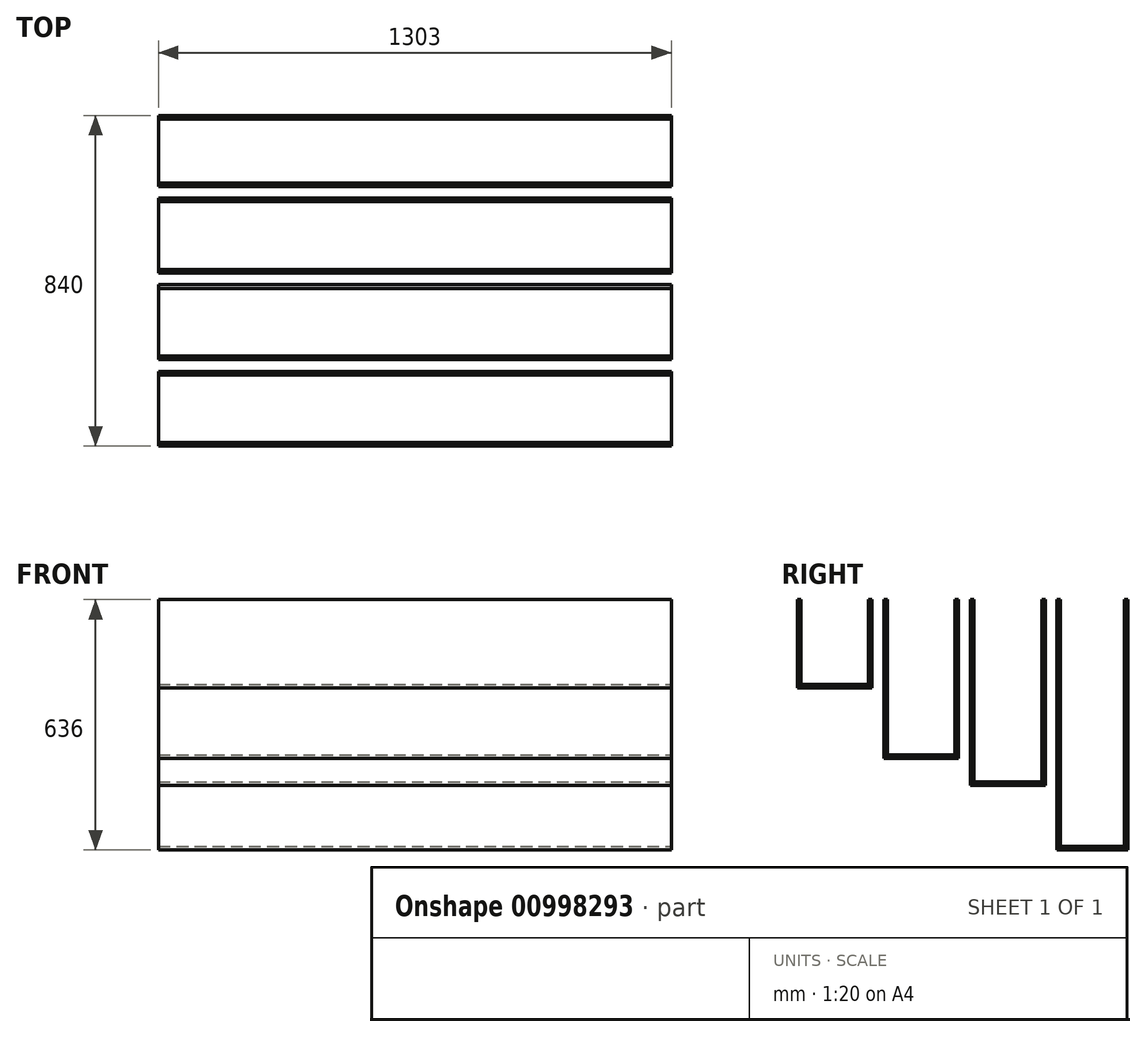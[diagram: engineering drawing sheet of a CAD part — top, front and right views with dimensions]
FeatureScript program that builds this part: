
annotation { "Feature Type Name" : "Feature", "Feature Type Description" : "" }
export const myFeature = defineFeature(function(context is Context, id is Id, definition is map)
    precondition{}
    {
        {
            var Q0;
            Q0=qCreatedBy(makeId("Right.planeOp"),FACE);
            var sketch = newSketch(context, id + "F0", { "sketchPlane" : qUnion([Q0])});
            skLineSegment(sketch, "E0.bottom", {"start": v(-47.02, 266.3) * mm, "end": v(-38.02, 266.3) * mm});
            skLineSegment(sketch, "E0.top", {"start": v(-47.02, 42.3) * mm, "end": v(-38.02, 42.3) * mm});
            skLineSegment(sketch, "E0.left", {"start": v(-47.02, 266.3) * mm, "end": v(-47.02, 42.3) * mm});
            skLineSegment(sketch, "E0.right", {"start": v(-38.02, 266.3) * mm, "end": v(-38.02, 42.3) * mm});
            skSolve(sketch);
        }
        {
            var Q0;
            Q0 = qSketchRegion(id + "F0", true);
            extrude(context, id + "F1", {"entities" : qUnion([Q0]), "oppositeDirection" : true, "depth" : 1303 * mm, "offsetDistance" : 25 * mm});
        }
        {
            var Q0;
            Q0=qCreatedBy(makeId("Right.planeOp"),FACE);
            var sketch = newSketch(context, id + "F2", { "sketchPlane" : qUnion([Q0])});
            skLineSegment(sketch, "E1.0.0", {"start": v(-47.02, 266.3) * mm, "end": v(-47.02, 42.3) * mm, "construction": true});
            skLineSegment(sketch, "E1.0.1", {"start": v(-47.02, 42.3) * mm, "end": v(-38.02, 42.3) * mm, "construction": true});
            skLineSegment(sketch, "E1.0.2", {"start": v(-38.02, 42.3) * mm, "end": v(-38.02, 266.3) * mm, "construction": true});
            skLineSegment(sketch, "E1.0.3", {"start": v(-38.02, 266.3) * mm, "end": v(-47.02, 266.3) * mm, "construction": true});
            skLineSegment(sketch, "E2.bottom", {"start": v(-38.02, 42.3) * mm, "end": v(133.98, 42.3) * mm});
            skLineSegment(sketch, "E2.top", {"start": v(-38.02, 51.3) * mm, "end": v(133.98, 51.3) * mm});
            skLineSegment(sketch, "E2.left", {"start": v(-38.02, 42.3) * mm, "end": v(-38.02, 51.3) * mm});
            skLineSegment(sketch, "E2.right", {"start": v(133.98, 42.3) * mm, "end": v(133.98, 51.3) * mm});
            skSolve(sketch);
        }
        {
            var Q0;
            Q0 = qSketchRegion(id + "F2", true);
            var Q1;
            Q1=makeQuery(id+"F1.opExtrude","CAP_FACE",FACE,{"disambiguationData":[OSD([sQuery(id+"F0.wireOp",EDGE,"E0.bottom"),sQuery(id+"F0.wireOp",EDGE,"E0.top"),sQuery(id+"F0.wireOp",EDGE,"E0.left"),sQuery(id+"F0.wireOp",EDGE,"E0.right")])],"isStart":false});
            extrude(context, id + "F3", {"entities" : qUnion([Q0]), "endBound" : BoundingType.UP_TO_SURFACE, "oppositeDirection" : true, "depth" : 1303 * mm, "endBoundEntityFace" : qUnion([Q1]), "offsetDistance" : 25 * mm});
        }
        {
            var Q0;
            Q0=qCreatedBy(makeId("Right.planeOp"),FACE);
            var sketch = newSketch(context, id + "F4", { "sketchPlane" : qUnion([Q0])});
            skLineSegment(sketch, "E3.0.0", {"start": v(133.98, 51.3) * mm, "end": v(-38.02, 51.3) * mm, "construction": true});
            skLineSegment(sketch, "E3.0.1", {"start": v(-38.02, 51.3) * mm, "end": v(-38.02, 42.3) * mm, "construction": true});
            skLineSegment(sketch, "E3.0.2", {"start": v(-38.02, 42.3) * mm, "end": v(133.98, 42.3) * mm, "construction": true});
            skLineSegment(sketch, "E3.0.3", {"start": v(133.98, 42.3) * mm, "end": v(133.98, 51.3) * mm, "construction": true});
            skLineSegment(sketch, "E4.bottom", {"start": v(133.98, 42.3) * mm, "end": v(142.98, 42.3) * mm});
            skLineSegment(sketch, "E4.top", {"start": v(133.98, 266.3) * mm, "end": v(142.98, 266.3) * mm});
            skLineSegment(sketch, "E4.left", {"start": v(133.98, 42.3) * mm, "end": v(133.98, 266.3) * mm});
            skLineSegment(sketch, "E4.right", {"start": v(142.98, 42.3) * mm, "end": v(142.98, 266.3) * mm});
            skSolve(sketch);
        }
        {
            var Q0;
            Q0 = qSketchRegion(id + "F4", true);
            var Q1;
            Q1=makeQuery(id+"F3.opExtrude","CAP_FACE",FACE,{"disambiguationData":[OSD([sQuery(id+"F2.wireOp",EDGE,"E2.bottom"),sQuery(id+"F2.wireOp",EDGE,"E2.top"),sQuery(id+"F2.wireOp",EDGE,"E2.left"),sQuery(id+"F2.wireOp",EDGE,"E2.right")])],"isStart":false});
            extrude(context, id + "F5", {"entities" : qUnion([Q0]), "endBound" : BoundingType.UP_TO_SURFACE, "oppositeDirection" : true, "depth" : 1303 * mm, "endBoundEntityFace" : qUnion([Q1]), "offsetDistance" : 25 * mm});
        }
        {
            var Q0;
            Q0=qCreatedBy(makeId("Right.planeOp"),FACE);
            var sketch = newSketch(context, id + "F6", { "sketchPlane" : qUnion([Q0])});
            skLineSegment(sketch, "E5.0.0", {"start": v(-41.02, 42.3) * mm, "end": v(142.98, 42.3) * mm, "construction": true});
            skLineSegment(sketch, "E5.0.1", {"start": v(142.98, 42.3) * mm, "end": v(142.98, 266.3) * mm, "construction": true});
            skLineSegment(sketch, "E5.0.2", {"start": v(142.98, 266.3) * mm, "end": v(133.98, 266.3) * mm, "construction": true});
            skLineSegment(sketch, "E5.0.3", {"start": v(133.98, 266.3) * mm, "end": v(133.98, 42.3) * mm, "construction": true});
            skLineSegment(sketch, "E5.0.4", {"start": v(133.98, 42.3) * mm, "end": v(-41.02, 42.3) * mm, "construction": true});
            skLineSegment(sketch, "E5.0.5", {"start": v(-41.02, 42.3) * mm, "end": v(-41.02, 42.3) * mm});
            skLineSegment(sketch, "E6.bottom", {"start": v(172.98, 266.3) * mm, "end": v(181.98, 266.3) * mm});
            skLineSegment(sketch, "E6.top", {"start": v(172.98, -137.7) * mm, "end": v(181.98, -137.7) * mm});
            skLineSegment(sketch, "E6.left", {"start": v(172.98, 266.3) * mm, "end": v(172.98, -137.7) * mm});
            skLineSegment(sketch, "E6.right", {"start": v(181.98, 266.3) * mm, "end": v(181.98, -137.7) * mm});
            skSolve(sketch);
        }
        {
            var Q0;
            Q0=makeQuery(id+"F6.imprint","IMPRINT",FACE,{"disambiguationData":[TD([[makeQuery(id+"F6.imprint","IMPRINT",EDGE,{"derivedFrom":sQuery(id+"F6.wireOp",EDGE,"E6.bottom")}),-1.0]])]});
            var Q1;
            Q1=makeQuery(id+"F5.opExtrude","CAP_FACE",FACE,{"disambiguationData":[OSD([sQuery(id+"F4.wireOp",EDGE,"E4.bottom"),sQuery(id+"F4.wireOp",EDGE,"E4.top"),sQuery(id+"F4.wireOp",EDGE,"E4.left"),sQuery(id+"F4.wireOp",EDGE,"E4.right")])],"isStart":false});
            extrude(context, id + "F7", {"entities" : qUnion([Q0]), "endBound" : BoundingType.UP_TO_SURFACE, "oppositeDirection" : true, "depth" : 1303 * mm, "endBoundEntityFace" : qUnion([Q1]), "offsetDistance" : 25 * mm});
        }
        {
            var Q0;
            Q0=qCreatedBy(makeId("Right.planeOp"),FACE);
            var sketch = newSketch(context, id + "F8", { "sketchPlane" : qUnion([Q0])});
            skLineSegment(sketch, "E7.0.0", {"start": v(172.98, 266.3) * mm, "end": v(172.98, -137.7) * mm, "construction": true});
            skLineSegment(sketch, "E7.0.1", {"start": v(172.98, -137.7) * mm, "end": v(181.98, -137.7) * mm, "construction": true});
            skLineSegment(sketch, "E7.0.2", {"start": v(181.98, -137.7) * mm, "end": v(181.98, 266.3) * mm, "construction": true});
            skLineSegment(sketch, "E7.0.3", {"start": v(181.98, 266.3) * mm, "end": v(172.98, 266.3) * mm, "construction": true});
            skLineSegment(sketch, "E8.bottom", {"start": v(181.98, -137.7) * mm, "end": v(353.98, -137.7) * mm});
            skLineSegment(sketch, "E8.top", {"start": v(181.98, -128.7) * mm, "end": v(353.98, -128.7) * mm});
            skLineSegment(sketch, "E8.left", {"start": v(181.98, -137.7) * mm, "end": v(181.98, -128.7) * mm});
            skLineSegment(sketch, "E8.right", {"start": v(353.98, -137.7) * mm, "end": v(353.98, -128.7) * mm});
            skSolve(sketch);
        }
        {
            var Q0;
            Q0 = qSketchRegion(id + "F8", true);
            var Q1;
            Q1=makeQuery(id+"F7.opExtrude","CAP_FACE",FACE,{"disambiguationData":[OSD([sQuery(id+"F6.wireOp",EDGE,"E6.bottom"),sQuery(id+"F6.wireOp",EDGE,"E6.top"),sQuery(id+"F6.wireOp",EDGE,"E6.left"),sQuery(id+"F6.wireOp",EDGE,"E6.right")])],"isStart":false});
            extrude(context, id + "F9", {"entities" : qUnion([Q0]), "endBound" : BoundingType.UP_TO_SURFACE, "oppositeDirection" : true, "depth" : 1303 * mm, "endBoundEntityFace" : qUnion([Q1]), "offsetDistance" : 25 * mm});
        }
        {
            var Q0;
            Q0=qCreatedBy(makeId("Right.planeOp"),FACE);
            var sketch = newSketch(context, id + "F10", { "sketchPlane" : qUnion([Q0])});
            skLineSegment(sketch, "E9.0.0", {"start": v(353.98, -128.7) * mm, "end": v(181.98, -128.7) * mm, "construction": true});
            skLineSegment(sketch, "E9.0.1", {"start": v(181.98, -128.7) * mm, "end": v(181.98, -137.7) * mm, "construction": true});
            skLineSegment(sketch, "E9.0.2", {"start": v(181.98, -137.7) * mm, "end": v(353.98, -137.7) * mm, "construction": true});
            skLineSegment(sketch, "E9.0.3", {"start": v(353.98, -137.7) * mm, "end": v(353.98, -128.7) * mm, "construction": true});
            skLineSegment(sketch, "E10.bottom", {"start": v(353.98, -137.7) * mm, "end": v(362.98, -137.7) * mm});
            skLineSegment(sketch, "E10.top", {"start": v(353.98, 266.3) * mm, "end": v(362.98, 266.3) * mm});
            skLineSegment(sketch, "E10.left", {"start": v(353.98, -137.7) * mm, "end": v(353.98, 266.3) * mm});
            skLineSegment(sketch, "E10.right", {"start": v(362.98, -137.7) * mm, "end": v(362.98, 266.3) * mm});
            skSolve(sketch);
        }
        {
            var Q0;
            Q0 = qSketchRegion(id + "F10", true);
            var Q1;
            Q1=makeQuery(id+"F9.opExtrude","CAP_FACE",FACE,{"disambiguationData":[OSD([sQuery(id+"F8.wireOp",EDGE,"E8.bottom"),sQuery(id+"F8.wireOp",EDGE,"E8.top"),sQuery(id+"F8.wireOp",EDGE,"E8.left"),sQuery(id+"F8.wireOp",EDGE,"E8.right")])],"isStart":false});
            extrude(context, id + "F11", {"entities" : qUnion([Q0]), "endBound" : BoundingType.UP_TO_SURFACE, "oppositeDirection" : true, "depth" : 1315 * mm, "endBoundEntityFace" : qUnion([Q1]), "offsetDistance" : 25 * mm});
        }
        {
            var Q0;
            Q0=qCreatedBy(makeId("Right.planeOp"),FACE);
            var sketch = newSketch(context, id + "F12", { "sketchPlane" : qUnion([Q0])});
            skLineSegment(sketch, "E11.0.0", {"start": v(362.98, 266.3) * mm, "end": v(353.98, 266.3) * mm, "construction": true});
            skLineSegment(sketch, "E11.0.1", {"start": v(353.98, 266.3) * mm, "end": v(353.98, -137.7) * mm, "construction": true});
            skLineSegment(sketch, "E11.0.2", {"start": v(353.98, -137.7) * mm, "end": v(362.98, -137.7) * mm, "construction": true});
            skLineSegment(sketch, "E11.0.3", {"start": v(362.98, -137.7) * mm, "end": v(362.98, 266.3) * mm, "construction": true});
            skLineSegment(sketch, "E12.bottom", {"start": v(392.98, 266.3) * mm, "end": v(401.98, 266.3) * mm});
            skLineSegment(sketch, "E12.top", {"start": v(392.98, -205.7) * mm, "end": v(401.98, -205.7) * mm});
            skLineSegment(sketch, "E12.left", {"start": v(392.98, 266.3) * mm, "end": v(392.98, -205.7) * mm});
            skLineSegment(sketch, "E12.right", {"start": v(401.98, 266.3) * mm, "end": v(401.98, -205.7) * mm});
            skSolve(sketch);
        }
        {
            var Q0;
            Q0 = qSketchRegion(id + "F12", true);
            var Q1;
            Q1=makeQuery(id+"F9.opExtrude","CAP_FACE",FACE,{"disambiguationData":[OSD([sQuery(id+"F8.wireOp",EDGE,"E8.bottom"),sQuery(id+"F8.wireOp",EDGE,"E8.top"),sQuery(id+"F8.wireOp",EDGE,"E8.left"),sQuery(id+"F8.wireOp",EDGE,"E8.right")])],"isStart":false});
            extrude(context, id + "F13", {"entities" : qUnion([Q0]), "endBound" : BoundingType.UP_TO_SURFACE, "oppositeDirection" : true, "depth" : 1315 * mm, "endBoundEntityFace" : qUnion([Q1]), "offsetDistance" : 25 * mm});
        }
        {
            var Q0;
            Q0=qCreatedBy(makeId("Right.planeOp"),FACE);
            var sketch = newSketch(context, id + "F14", { "sketchPlane" : qUnion([Q0])});
            skLineSegment(sketch, "E13.0.0", {"start": v(392.98, 266.3) * mm, "end": v(392.98, -205.7) * mm, "construction": true});
            skLineSegment(sketch, "E13.0.1", {"start": v(392.98, -205.7) * mm, "end": v(401.98, -205.7) * mm, "construction": true});
            skLineSegment(sketch, "E13.0.2", {"start": v(401.98, -205.7) * mm, "end": v(401.98, 266.3) * mm, "construction": true});
            skLineSegment(sketch, "E13.0.3", {"start": v(401.98, 266.3) * mm, "end": v(392.98, 266.3) * mm, "construction": true});
            skLineSegment(sketch, "E14.bottom", {"start": v(401.98, -205.7) * mm, "end": v(573.98, -205.7) * mm});
            skLineSegment(sketch, "E14.top", {"start": v(401.98, -196.7) * mm, "end": v(573.98, -196.7) * mm});
            skLineSegment(sketch, "E14.left", {"start": v(401.98, -205.7) * mm, "end": v(401.98, -196.7) * mm});
            skLineSegment(sketch, "E14.right", {"start": v(573.98, -205.7) * mm, "end": v(573.98, -196.7) * mm});
            skSolve(sketch);
        }
        {
            var Q0;
            Q0 = qSketchRegion(id + "F14", true);
            var Q1;
            Q1=makeQuery(id+"F13.opExtrude","CAP_FACE",FACE,{"disambiguationData":[OSD([sQuery(id+"F12.wireOp",EDGE,"E12.bottom"),sQuery(id+"F12.wireOp",EDGE,"E12.top"),sQuery(id+"F12.wireOp",EDGE,"E12.left"),sQuery(id+"F12.wireOp",EDGE,"E12.right")])],"isStart":false});
            extrude(context, id + "F15", {"entities" : qUnion([Q0]), "endBound" : BoundingType.UP_TO_SURFACE, "oppositeDirection" : true, "depth" : 1315 * mm, "endBoundEntityFace" : qUnion([Q1]), "offsetDistance" : 25 * mm});
        }
        {
            var Q0;
            Q0=makeQuery(id+"F15.opExtrude","CAP_FACE",FACE,{"disambiguationData":[OSD([sQuery(id+"F14.wireOp",EDGE,"E14.bottom"),sQuery(id+"F14.wireOp",EDGE,"E14.top"),sQuery(id+"F14.wireOp",EDGE,"E14.left"),sQuery(id+"F14.wireOp",EDGE,"E14.right")])],"isStart":true});
            var sketch = newSketch(context, id + "F16", { "sketchPlane" : qUnion([Q0])});
            skLineSegment(sketch, "E15.bottom", {"start": v(573.98, -205.7) * mm, "end": v(582.98, -205.7) * mm});
            skLineSegment(sketch, "E15.top", {"start": v(573.98, 266.3) * mm, "end": v(582.98, 266.3) * mm});
            skLineSegment(sketch, "E15.left", {"start": v(573.98, -205.7) * mm, "end": v(573.98, 266.3) * mm});
            skLineSegment(sketch, "E15.right", {"start": v(582.98, -205.7) * mm, "end": v(582.98, 266.3) * mm});
            skSolve(sketch);
        }
        {
            var Q0;
            Q0 = qSketchRegion(id + "F16", true);
            var Q1;
            Q1=makeQuery(id+"F15.opExtrude","CAP_FACE",FACE,{"disambiguationData":[OSD([sQuery(id+"F14.wireOp",EDGE,"E14.bottom"),sQuery(id+"F14.wireOp",EDGE,"E14.top"),sQuery(id+"F14.wireOp",EDGE,"E14.left"),sQuery(id+"F14.wireOp",EDGE,"E14.right")])],"isStart":false});
            extrude(context, id + "F17", {"entities" : qUnion([Q0]), "endBound" : BoundingType.UP_TO_SURFACE, "oppositeDirection" : true, "depth" : 1315 * mm, "endBoundEntityFace" : qUnion([Q1]), "offsetDistance" : 25 * mm});
        }
        {
            var Q0;
            Q0=makeQuery(id+"F17.opExtrude","CAP_FACE",FACE,{"disambiguationData":[OSD([sQuery(id+"F16.wireOp",EDGE,"E15.bottom"),sQuery(id+"F16.wireOp",EDGE,"E15.top"),sQuery(id+"F16.wireOp",EDGE,"E15.left"),sQuery(id+"F16.wireOp",EDGE,"E15.right")])],"isStart":true});
            var sketch = newSketch(context, id + "F18", { "sketchPlane" : qUnion([Q0])});
            skLineSegment(sketch, "E16.bottom", {"start": v(612.98, 266.3) * mm, "end": v(621.98, 266.3) * mm});
            skLineSegment(sketch, "E16.top", {"start": v(612.98, -369.7) * mm, "end": v(621.98, -369.7) * mm});
            skLineSegment(sketch, "E16.left", {"start": v(612.98, 266.3) * mm, "end": v(612.98, -369.7) * mm});
            skLineSegment(sketch, "E16.right", {"start": v(621.98, 266.3) * mm, "end": v(621.98, -369.7) * mm});
            skSolve(sketch);
        }
        {
            var Q0;
            Q0 = qSketchRegion(id + "F18", true);
            var Q1;
            Q1=makeQuery(id+"F17.opExtrude","CAP_FACE",FACE,{"disambiguationData":[OSD([sQuery(id+"F16.wireOp",EDGE,"E15.bottom"),sQuery(id+"F16.wireOp",EDGE,"E15.top"),sQuery(id+"F16.wireOp",EDGE,"E15.left"),sQuery(id+"F16.wireOp",EDGE,"E15.right")])],"isStart":false});
            extrude(context, id + "F19", {"entities" : qUnion([Q0]), "endBound" : BoundingType.UP_TO_SURFACE, "oppositeDirection" : true, "depth" : 1315 * mm, "endBoundEntityFace" : qUnion([Q1]), "offsetDistance" : 25 * mm});
        }
        {
            var Q0;
            Q0=makeQuery(id+"F19.opExtrude","CAP_FACE",FACE,{"disambiguationData":[OSD([sQuery(id+"F18.wireOp",EDGE,"E16.bottom"),sQuery(id+"F18.wireOp",EDGE,"E16.top"),sQuery(id+"F18.wireOp",EDGE,"E16.left"),sQuery(id+"F18.wireOp",EDGE,"E16.right")])],"isStart":true});
            var sketch = newSketch(context, id + "F20", { "sketchPlane" : qUnion([Q0])});
            skLineSegment(sketch, "E17.bottom", {"start": v(621.98, -369.7) * mm, "end": v(783.98, -369.7) * mm});
            skLineSegment(sketch, "E17.top", {"start": v(621.98, -360.7) * mm, "end": v(783.98, -360.7) * mm});
            skLineSegment(sketch, "E17.left", {"start": v(621.98, -369.7) * mm, "end": v(621.98, -360.7) * mm});
            skLineSegment(sketch, "E17.right", {"start": v(783.98, -369.7) * mm, "end": v(783.98, -360.7) * mm});
            skSolve(sketch);
        }
        {
            var Q0;
            Q0 = qSketchRegion(id + "F20", true);
            var Q1;
            Q1=makeQuery(id+"F19.opExtrude","CAP_FACE",FACE,{"disambiguationData":[OSD([sQuery(id+"F18.wireOp",EDGE,"E16.bottom"),sQuery(id+"F18.wireOp",EDGE,"E16.top"),sQuery(id+"F18.wireOp",EDGE,"E16.left"),sQuery(id+"F18.wireOp",EDGE,"E16.right")])],"isStart":false});
            extrude(context, id + "F21", {"entities" : qUnion([Q0]), "endBound" : BoundingType.UP_TO_SURFACE, "oppositeDirection" : true, "depth" : 1315 * mm, "endBoundEntityFace" : qUnion([Q1]), "offsetDistance" : 25 * mm});
        }
        {
            var Q0;
            Q0=makeQuery(id+"F21.opExtrude","CAP_FACE",FACE,{"disambiguationData":[OSD([sQuery(id+"F20.wireOp",EDGE,"E17.bottom"),sQuery(id+"F20.wireOp",EDGE,"E17.top"),sQuery(id+"F20.wireOp",EDGE,"E17.left"),sQuery(id+"F20.wireOp",EDGE,"E17.right")])],"isStart":true});
            var sketch = newSketch(context, id + "F22", { "sketchPlane" : qUnion([Q0])});
            skLineSegment(sketch, "E18.bottom", {"start": v(783.98, -369.7) * mm, "end": v(792.98, -369.7) * mm});
            skLineSegment(sketch, "E18.top", {"start": v(783.98, 266.3) * mm, "end": v(792.98, 266.3) * mm});
            skLineSegment(sketch, "E18.left", {"start": v(783.98, -369.7) * mm, "end": v(783.98, 266.3) * mm});
            skLineSegment(sketch, "E18.right", {"start": v(792.98, -369.7) * mm, "end": v(792.98, 266.3) * mm});
            skSolve(sketch);
        }
        {
            var Q0;
            Q0 = qSketchRegion(id + "F6", true);
            var Q1;
            Q1 = qSketchRegion(id + "F22", true);
            var Q2;
            Q2=makeQuery(id+"F21.opExtrude","CAP_FACE",FACE,{"disambiguationData":[OSD([sQuery(id+"F20.wireOp",EDGE,"E17.bottom"),sQuery(id+"F20.wireOp",EDGE,"E17.top"),sQuery(id+"F20.wireOp",EDGE,"E17.left"),sQuery(id+"F20.wireOp",EDGE,"E17.right")])],"isStart":false});
            extrude(context, id + "F23", {"entities" : qUnion([Q0, Q1]), "endBound" : BoundingType.UP_TO_SURFACE, "oppositeDirection" : true, "depth" : 1315 * mm, "endBoundEntityFace" : qUnion([Q2]), "offsetDistance" : 25 * mm});
        }
    });
